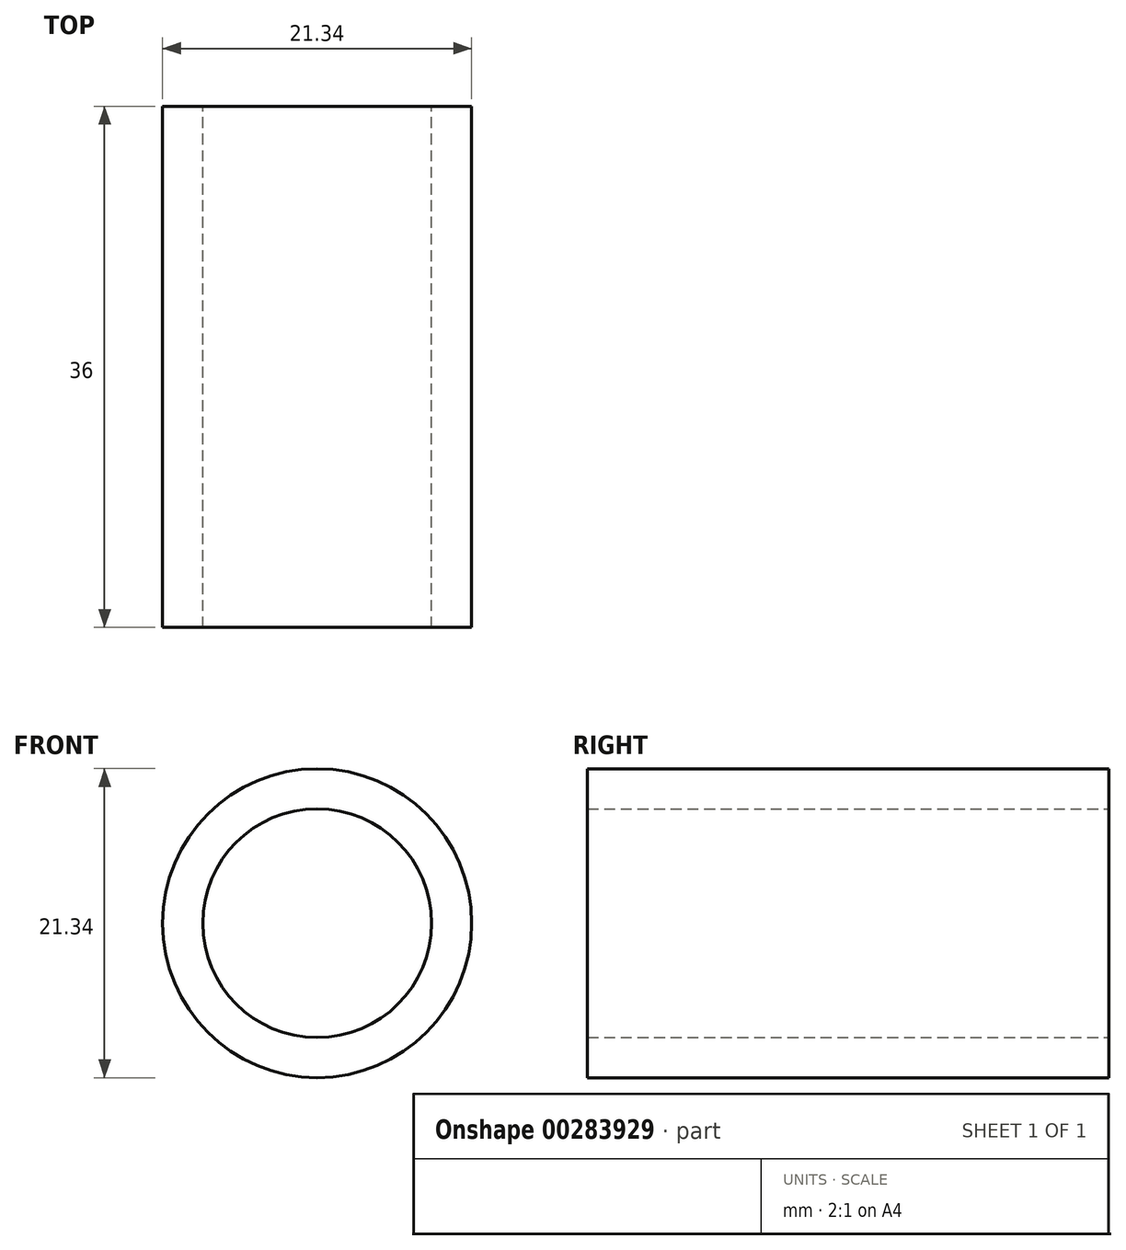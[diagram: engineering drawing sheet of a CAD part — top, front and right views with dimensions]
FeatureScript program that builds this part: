
annotation { "Feature Type Name" : "Feature", "Feature Type Description" : "" }
export const myFeature = defineFeature(function(context is Context, id is Id, definition is map)
    precondition{}
    {
        {
            var Q0;
            Q0=qCreatedBy(makeId("Front.planeOp"),FACE);
            var sketch = newSketch(context, id + "F0", { "sketchPlane" : qUnion([Q0])});
            skCircle(sketch, "E0", {"center": v(0, 0) * mm, "radius": 7.9 * mm});
            skCircle(sketch, "E1", {"center": v(0, 0) * mm, "radius": 10.67 * mm});
            skSolve(sketch);
        }
        {
            var Q0;
            Q0=qSketchRegion(id+"F0",true);
            extrude(context, id + "F1", {"entities" : qUnion([Q0]), "endBound" : BoundingType.SYMMETRIC, "depth" : 36 * mm});
        }
    });
